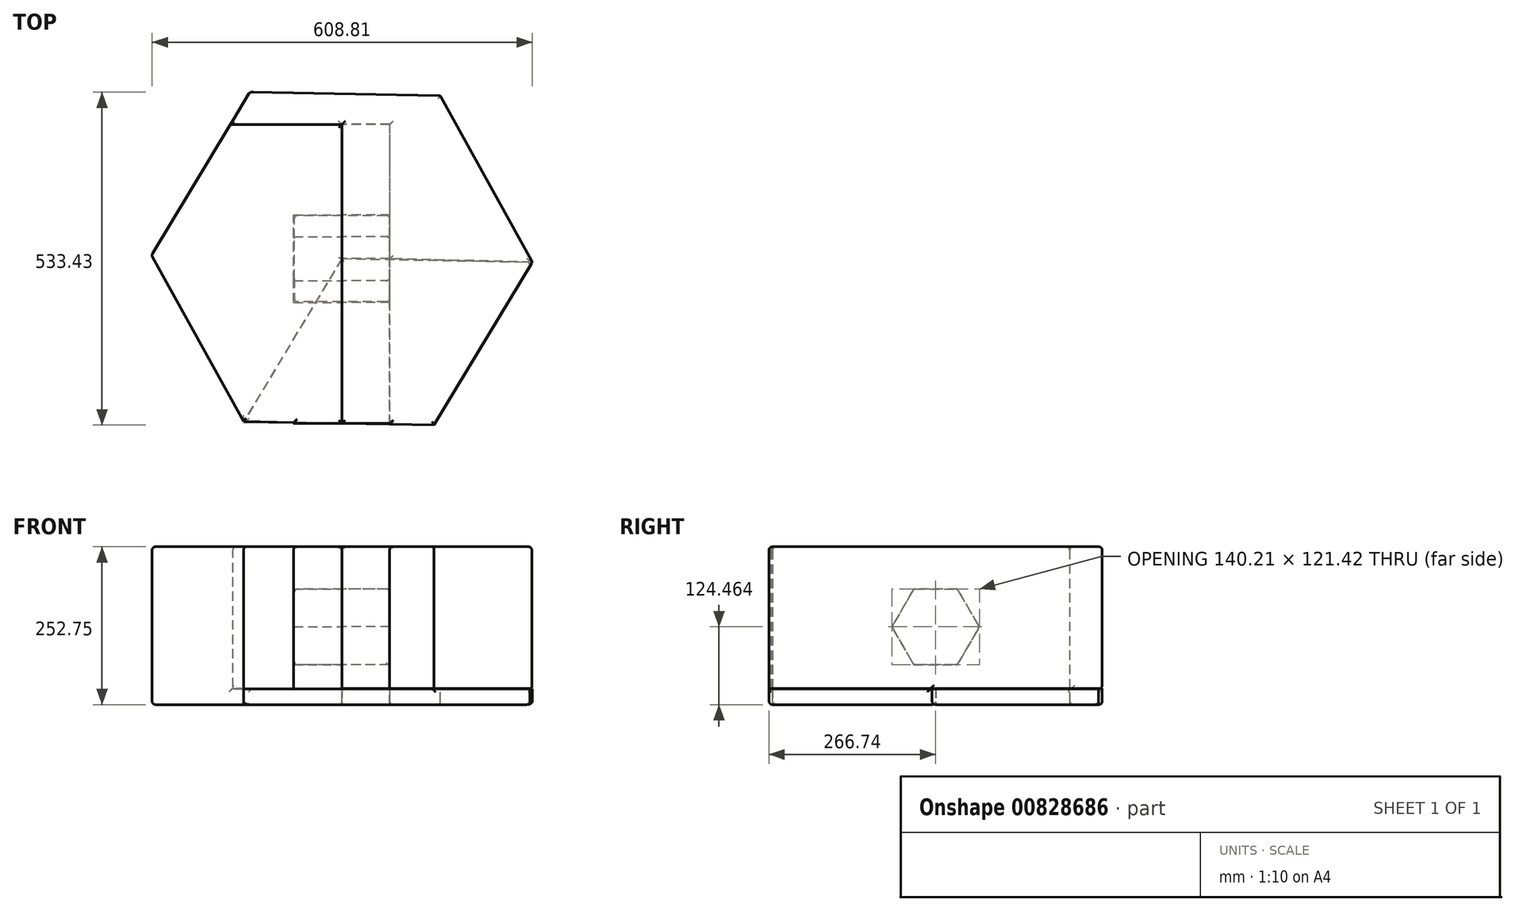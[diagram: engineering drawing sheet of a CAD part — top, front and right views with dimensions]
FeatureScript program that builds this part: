
annotation { "Feature Type Name" : "Feature", "Feature Type Description" : "" }
export const myFeature = defineFeature(function(context is Context, id is Id, definition is map)
    precondition{}
    {
        {
            var Q0;
            Q0=qCreatedBy(makeId("Top.planeOp"),FACE);
            var sketch = newSketch(context, id + "F0", { "sketchPlane" : qUnion([Q0])});
            skCircle(sketch, "E0.cCircle", {"center": v(0, 0) * mm, "radius": 264 * mm, "construction": true});
            skLineSegment(sketch, "E0.0", {"start": v(157.21, 261.19) * mm, "end": v(304.8, -5.56) * mm});
            skLineSegment(sketch, "E0.1", {"start": v(304.8, -5.56) * mm, "end": v(147.59, -266.74) * mm});
            skLineSegment(sketch, "E0.2", {"start": v(147.59, -266.74) * mm, "end": v(-157.21, -261.19) * mm});
            skLineSegment(sketch, "E0.3", {"start": v(-157.21, -261.19) * mm, "end": v(-304.8, 5.56) * mm});
            skLineSegment(sketch, "E0.4", {"start": v(-304.8, 5.56) * mm, "end": v(-147.59, 266.74) * mm});
            skLineSegment(sketch, "E0.5", {"start": v(-147.59, 266.74) * mm, "end": v(157.21, 261.19) * mm});
            skPoint(sketch, "E0.0.midPoint", {"position": v(231, 127.81) * mm});
            skSolve(sketch);
        }
        {
            var Q0;
            Q0=makeQuery(id+"F0.imprint","IMPRINT",FACE,{"disambiguationData":[TD([[makeQuery(id+"F0.imprint","IMPRINT",EDGE,{"derivedFrom":sQuery(id+"F0.wireOp",EDGE,"E0.0")}),-1.0]])]});
            var sketch = newSketch(context, id + "F1", { "sketchPlane" : qUnion([Q0])});
            skLineSegment(sketch, "E1", {"start": v(0, 0) * mm, "end": v(-157.21, -261.19) * mm});
            skLineSegment(sketch, "E2", {"start": v(0, 0) * mm, "end": v(304.8, -5.56) * mm});
            skLineSegment(sketch, "E3", {"start": v(304.8, -5.56) * mm, "end": v(147.59, -266.74) * mm});
            skLineSegment(sketch, "E4", {"start": v(147.59, -266.74) * mm, "end": v(-157.21, -261.19) * mm});
            skSolve(sketch);
        }
        {
            var Q0;
            Q0=makeQuery(id+"F1.imprint","IMPRINT",FACE,{"disambiguationData":[TD([[makeQuery(id+"F1.imprint","IMPRINT",EDGE,{"derivedFrom":sQuery(id+"F1.wireOp",EDGE,"E1")}),1.0]])]});
            extrude(context, id + "F2", {"entities" : qUnion([Q0]), "depth" : 25.4 * mm, "offsetDistance" : 25.4 * mm});
        }
        {
            var Q0;
            Q0=qCreatedBy(makeId("Right.planeOp"),FACE);
            var sketch = newSketch(context, id + "F3", { "sketchPlane" : qUnion([Q0])});
            skCircle(sketch, "E5.cCircle", {"center": v(0, 124.43) * mm, "radius": 60.5 * mm, "construction": true});
            skLineSegment(sketch, "E5.0", {"start": v(-34.92, 184.92) * mm, "end": v(34.92, 184.92) * mm});
            skLineSegment(sketch, "E5.1", {"start": v(34.92, 184.92) * mm, "end": v(69.85, 124.43) * mm});
            skLineSegment(sketch, "E5.2", {"start": v(69.85, 124.43) * mm, "end": v(34.93, 63.94) * mm});
            skLineSegment(sketch, "E5.3", {"start": v(34.93, 63.94) * mm, "end": v(-34.92, 63.94) * mm});
            skLineSegment(sketch, "E5.4", {"start": v(-34.92, 63.94) * mm, "end": v(-69.85, 124.43) * mm});
            skLineSegment(sketch, "E5.5", {"start": v(-69.85, 124.43) * mm, "end": v(-34.92, 184.92) * mm});
            skPoint(sketch, "E5.0.midPoint", {"position": v(0, 184.92) * mm});
            skSolve(sketch);
        }
        {
            var Q0;
            Q0 = qSketchRegion(id + "F3", true);
            extrude(context, id + "F4", {"entities" : qUnion([Q0]), "depth" : 76.2 * mm, "offsetDistance" : 25.4 * mm, "hasSecondDirection" : true, "secondDirectionOppositeDirection" : true, "secondDirectionDepth" : 76.2 * mm});
        }
        {
            var Q0;
            Q0=qCreatedBy(makeId("Right.planeOp"),FACE);
            var sketch = newSketch(context, id + "F5", { "sketchPlane" : qUnion([Q0])});
            skLineSegment(sketch, "E6", {"start": v(-264.07, 25.84) * mm, "end": v(0.25, 25.84) * mm});
            skLineSegment(sketch, "E7", {"start": v(0.25, 25.84) * mm, "end": v(0.25, 0) * mm});
            skLineSegment(sketch, "E8", {"start": v(0.25, 0) * mm, "end": v(214.97, 0) * mm});
            skLineSegment(sketch, "E9", {"start": v(214.97, 0) * mm, "end": v(214.97, 252.75) * mm});
            skLineSegment(sketch, "E10", {"start": v(214.97, 252.75) * mm, "end": v(-203.9, 252.75) * mm});
            skLineSegment(sketch, "E11", {"start": v(-203.9, 252.75) * mm, "end": v(-203.9, 88.98) * mm});
            skLineSegment(sketch, "E12", {"start": v(-203.9, 88.98) * mm, "end": v(-264.07, 88.98) * mm});
            skLineSegment(sketch, "E13", {"start": v(-264.07, 88.98) * mm, "end": v(-264.07, 25.84) * mm});
            skCircle(sketch, "E14.cCircle", {"center": v(0, 124.46) * mm, "radius": 60.71 * mm, "construction": true});
            skLineSegment(sketch, "E14.0", {"start": v(35.05, 185.18) * mm, "end": v(70.1, 124.46) * mm});
            skLineSegment(sketch, "E14.1", {"start": v(70.1, 124.46) * mm, "end": v(35.05, 63.75) * mm});
            skLineSegment(sketch, "E14.2", {"start": v(35.05, 63.75) * mm, "end": v(-35.05, 63.75) * mm});
            skLineSegment(sketch, "E14.3", {"start": v(-35.05, 63.75) * mm, "end": v(-70.1, 124.46) * mm});
            skLineSegment(sketch, "E14.4", {"start": v(-70.1, 124.46) * mm, "end": v(-35.05, 185.18) * mm});
            skLineSegment(sketch, "E14.5", {"start": v(-35.05, 185.18) * mm, "end": v(35.05, 185.18) * mm});
            skPoint(sketch, "E14.0.midPoint", {"position": v(52.58, 154.82) * mm});
            skSolve(sketch);
        }
        {
            var Q0;
            Q0=makeQuery(id+"F5.imprint","IMPRINT",FACE,{"disambiguationData":[TD([[makeQuery(id+"F5.imprint","IMPRINT",EDGE,{"derivedFrom":sQuery(id+"F5.wireOp",EDGE,"E6")}),1.0]])]});
            extrude(context, id + "F6", {"entities" : qUnion([Q0]), "depth" : 76.45 * mm, "offsetDistance" : 25.4 * mm});
        }
        {
            var Q0;
            Q0=makeQuery(id+"F6.opExtrude","SWEPT_FACE",FACE,{"disambiguationData":[OSD([sQuery(id+"F5.wireOp",EDGE,"E10")])]});
            var sketch = newSketch(context, id + "F7", { "sketchPlane" : qUnion([Q0])});
            skLineSegment(sketch, "E15", {"start": v(0, 214.97) * mm, "end": v(-178.75, 214.97) * mm});
            skLineSegment(sketch, "E16", {"start": v(-178.75, 214.97) * mm, "end": v(-147.59, 266.74) * mm});
            skLineSegment(sketch, "E17", {"start": v(-147.59, 266.74) * mm, "end": v(157.21, 261.19) * mm});
            skLineSegment(sketch, "E18", {"start": v(157.21, 261.19) * mm, "end": v(304.8, -5.56) * mm});
            skLineSegment(sketch, "E19", {"start": v(304.8, -5.56) * mm, "end": v(147.59, -266.74) * mm});
            skLineSegment(sketch, "E20", {"start": v(147.59, -266.74) * mm, "end": v(76.45, -265.45) * mm});
            skLineSegment(sketch, "E21", {"start": v(76.45, 214.97) * mm, "end": v(76.45, -265.45) * mm});
            skSolve(sketch);
        }
        {
            var Q0;
            Q0=makeQuery(id+"F7.imprint","IMPRINT",FACE,{"disambiguationData":[TD([[makeQuery(id+"F7.imprint","IMPRINT",EDGE,{"derivedFrom":sQuery(id+"F7.wireOp",EDGE,"E15")}),-1.0]])]});
            extrude(context, id + "F8", {"entities" : qUnion([Q0]), "operationType" : NewBodyOperationType.ADD, "oppositeDirection" : true, "depth" : 227.15 * mm, "offsetDistance" : 25.4 * mm});
        }
        {
            var Q0;
            Q0=makeQuery(id+"F2.opExtrude","CAP_FACE",FACE,{"disambiguationData":[OSD([sQuery(id+"F1.wireOp",EDGE,"E1"),sQuery(id+"F1.wireOp",EDGE,"E2"),sQuery(id+"F1.wireOp",EDGE,"E3"),sQuery(id+"F1.wireOp",EDGE,"E4")])],"isStart":false});
            var sketch = newSketch(context, id + "F9", { "sketchPlane" : qUnion([Q0])});
            skLineSegment(sketch, "E22", {"start": v(-157.34, -260.96) * mm, "end": v(-304.8, 5.56) * mm});
            skLineSegment(sketch, "E23", {"start": v(-304.8, 5.56) * mm, "end": v(-147.59, 266.74) * mm});
            skLineSegment(sketch, "E24", {"start": v(-147.59, 266.74) * mm, "end": v(157.21, 261.19) * mm});
            skLineSegment(sketch, "E25", {"start": v(157.21, 261.19) * mm, "end": v(304.8, -5.54) * mm});
            skLineSegment(sketch, "E26", {"start": v(304.8, -5.54) * mm, "end": v(76.7, 0) * mm});
            skLineSegment(sketch, "E27", {"start": v(76.7, 0) * mm, "end": v(76.7, 215.22) * mm});
            skLineSegment(sketch, "E28", {"start": v(76.7, 215.22) * mm, "end": v(-0.25, 215.22) * mm});
            skLineSegment(sketch, "E29", {"start": v(-0.25, 215.22) * mm, "end": v(-0.25, 0) * mm});
            skLineSegment(sketch, "E30", {"start": v(-0.25, 0) * mm, "end": v(-157.34, -260.96) * mm});
            skSolve(sketch);
        }
        {
            var Q0;
            Q0=makeQuery(id+"F9.imprint","IMPRINT",FACE,{"disambiguationData":[TD([[makeQuery(id+"F9.imprint","IMPRINT",EDGE,{"derivedFrom":sQuery(id+"F9.wireOp",EDGE,"E22")}),-1.0]])]});
            var Q1;
            Q1=makeQuery(id+"F2.opExtrude","CAP_FACE",FACE,{"disambiguationData":[OSD([sQuery(id+"F1.wireOp",EDGE,"E1"),sQuery(id+"F1.wireOp",EDGE,"E2"),sQuery(id+"F1.wireOp",EDGE,"E3"),sQuery(id+"F1.wireOp",EDGE,"E4")])],"isStart":true});
            extrude(context, id + "F10", {"entities" : qUnion([Q0]), "endBound" : BoundingType.UP_TO_SURFACE, "oppositeDirection" : true, "depth" : 25.4 * mm, "endBoundEntityFace" : qUnion([Q1]), "offsetDistance" : 25.4 * mm});
        }
        {
            var Q0;
            Q0=makeQuery(id+"F6.opExtrude","CAP_FACE",FACE,{"disambiguationData":[OSD([sQuery(id+"F5.wireOp",EDGE,"E6"),sQuery(id+"F5.wireOp",EDGE,"E7"),sQuery(id+"F5.wireOp",EDGE,"E8"),sQuery(id+"F5.wireOp",EDGE,"E9"),sQuery(id+"F5.wireOp",EDGE,"E10"),sQuery(id+"F5.wireOp",EDGE,"E11"),sQuery(id+"F5.wireOp",EDGE,"E12"),sQuery(id+"F5.wireOp",EDGE,"E13"),sQuery(id+"F5.wireOp",EDGE,"E14.0"),sQuery(id+"F5.wireOp",EDGE,"E14.1"),sQuery(id+"F5.wireOp",EDGE,"E14.2"),sQuery(id+"F5.wireOp",EDGE,"E14.3"),sQuery(id+"F5.wireOp",EDGE,"E14.4"),sQuery(id+"F5.wireOp",EDGE,"E14.5")])],"isStart":true});
            cPlane(context, id + "F11", {"entities" : qUnion([Q0]), "cplaneType" : CPlaneType.OFFSET, "offset" : 0.25 * mm, "width" : 152.4 * mm, "height" : 152.4 * mm});
        }
        {
            var Q0;
            Q0=qCreatedBy(id+"F11.planeOp",FACE);
            var sketch = newSketch(context, id + "F12", { "sketchPlane" : qUnion([Q0])});
            skLineSegment(sketch, "E31.bottom", {"start": v(-214.71, 252.75) * mm, "end": v(263.84, 252.75) * mm});
            skLineSegment(sketch, "E31.top", {"start": v(-214.71, 25.4) * mm, "end": v(263.84, 25.4) * mm});
            skLineSegment(sketch, "E31.left", {"start": v(-214.71, 252.75) * mm, "end": v(-214.71, 25.4) * mm});
            skLineSegment(sketch, "E31.right", {"start": v(263.84, 252.75) * mm, "end": v(263.84, 25.4) * mm});
            skCircle(sketch, "E32.cCircle", {"center": v(0, 124.46) * mm, "radius": 60.71 * mm, "construction": true});
            skLineSegment(sketch, "E32.0", {"start": v(-35.05, 185.18) * mm, "end": v(35.05, 185.18) * mm});
            skLineSegment(sketch, "E32.1", {"start": v(35.05, 185.18) * mm, "end": v(70.1, 124.46) * mm});
            skLineSegment(sketch, "E32.2", {"start": v(70.1, 124.46) * mm, "end": v(35.05, 63.75) * mm});
            skLineSegment(sketch, "E32.3", {"start": v(35.05, 63.75) * mm, "end": v(-35.05, 63.75) * mm});
            skLineSegment(sketch, "E32.4", {"start": v(-35.05, 63.75) * mm, "end": v(-70.1, 124.46) * mm});
            skLineSegment(sketch, "E32.5", {"start": v(-70.1, 124.46) * mm, "end": v(-35.05, 185.18) * mm});
            skPoint(sketch, "E32.0.midPoint", {"position": v(0, 185.18) * mm});
            skSolve(sketch);
        }
        {
            var Q0;
            Q0=makeQuery(id+"F12.imprint","IMPRINT",FACE,{"disambiguationData":[TD([[makeQuery(id+"F12.imprint","IMPRINT",EDGE,{"derivedFrom":sQuery(id+"F12.wireOp",EDGE,"E31.bottom")}),-1.0]])]});
            extrude(context, id + "F13", {"entities" : qUnion([Q0]), "depth" : 77.22 * mm, "offsetDistance" : 25.4 * mm});
        }
        {
            var Q0;
            Q0=makeQuery(id+"F10.opExtrude","CAP_FACE",FACE,{"disambiguationData":[OSD([sQuery(id+"F9.wireOp",EDGE,"E22"),sQuery(id+"F9.wireOp",EDGE,"E23"),sQuery(id+"F9.wireOp",EDGE,"E24"),sQuery(id+"F9.wireOp",EDGE,"E25"),sQuery(id+"F9.wireOp",EDGE,"E26"),sQuery(id+"F9.wireOp",EDGE,"E27"),sQuery(id+"F9.wireOp",EDGE,"E28"),sQuery(id+"F9.wireOp",EDGE,"E29"),sQuery(id+"F9.wireOp",EDGE,"E30")])],"isStart":true});
            var sketch = newSketch(context, id + "F14", { "sketchPlane" : qUnion([Q0])});
            skLineSegment(sketch, "E33", {"start": v(-304.8, 5.56) * mm, "end": v(-178.9, 214.71) * mm});
            skLineSegment(sketch, "E34", {"start": v(-178.9, 214.71) * mm, "end": v(-77.22, 214.71) * mm});
            skLineSegment(sketch, "E35", {"start": v(-77.22, 214.71) * mm, "end": v(-77.22, -262.42) * mm});
            skLineSegment(sketch, "E36", {"start": v(-157.34, -260.96) * mm, "end": v(-304.8, 5.56) * mm});
            skLineSegment(sketch, "E37", {"start": v(-77.22, -262.42) * mm, "end": v(-157.34, -260.96) * mm});
            skSolve(sketch);
        }
        {
            var Q0;
            Q0 = qSketchRegion(id + "F14", true);
            var Q1;
            Q1=makeQuery(id+"F13.opExtrude","SWEPT_FACE",FACE,{"disambiguationData":[OSD([sQuery(id+"F12.wireOp",EDGE,"E31.bottom")])]});
            extrude(context, id + "F15", {"entities" : qUnion([Q0]), "operationType" : NewBodyOperationType.ADD, "endBound" : BoundingType.UP_TO_SURFACE, "depth" : 25.4 * mm, "endBoundEntityFace" : qUnion([Q1]), "offsetDistance" : 25.4 * mm});
        }
        {
            var Q0;
            Q0=makeQuery(id+"F6.opExtrude","SWEPT_FACE",FACE,{"disambiguationData":[OSD([sQuery(id+"F5.wireOp",EDGE,"E12")])]});
            var sketch = newSketch(context, id + "F16", { "sketchPlane" : qUnion([Q0])});
            skLineSegment(sketch, "E38.bottom", {"start": v(0, -203.9) * mm, "end": v(76.45, -203.9) * mm});
            skLineSegment(sketch, "E38.top", {"start": v(0, -264.07) * mm, "end": v(76.45, -264.07) * mm});
            skLineSegment(sketch, "E38.left", {"start": v(0, -203.9) * mm, "end": v(0, -264.07) * mm});
            skLineSegment(sketch, "E38.right", {"start": v(76.45, -203.9) * mm, "end": v(76.45, -264.07) * mm});
            skSolve(sketch);
        }
        {
            var Q0;
            Q0 = qSketchRegion(id + "F16", true);
            var Q1;
            Q1=makeQuery(id+"F2.opExtrude","CAP_FACE",FACE,{"disambiguationData":[OSD([sQuery(id+"F1.wireOp",EDGE,"E1"),sQuery(id+"F1.wireOp",EDGE,"E2"),sQuery(id+"F1.wireOp",EDGE,"E3"),sQuery(id+"F1.wireOp",EDGE,"E4")])],"isStart":true});
            var Q2;
            Q2=makeQuery(id+"F8.opExtrude","CAP_VERTEX",VERTEX,{"disambiguationData":[OSD([sQuery(id+"F7.wireOp",EDGE,"E20"),sQuery(id+"F7.wireOp",EDGE,"E21")])],"isStart":true});
            extrude(context, id + "F17", {"entities" : qUnion([Q0]), "operationType" : NewBodyOperationType.ADD, "endBound" : BoundingType.UP_TO_VERTEX, "depth" : 25.4 * mm, "endBoundEntityFace" : qUnion([Q1]), "endBoundEntityVertex" : qUnion([Q2]), "offsetDistance" : 25.4 * mm});
        }
        {
            var Q0;
            Q0=makeQuery(id+"F15.boolean.opBoolean","MERGE",FACE,{"derivedFrom":[makeQuery(id+"F13.opExtrude","SWEPT_FACE",FACE,{"disambiguationData":[OSD([sQuery(id+"F12.wireOp",EDGE,"E31.bottom")])]}),makeQuery(id+"F15.opExtrude","CAP_FACE",FACE,{"disambiguationData":[OSD([sQuery(id+"F14.wireOp",EDGE,"E33"),sQuery(id+"F14.wireOp",EDGE,"E34"),sQuery(id+"F14.wireOp",EDGE,"E35"),sQuery(id+"F14.wireOp",EDGE,"E36"),sQuery(id+"F14.wireOp",EDGE,"E37")])],"isStart":false})]});
            var Q1;
            Q1=makeQuery(id+"F15.boolean.opBoolean","MERGE",FACE,{"derivedFrom":[makeQuery(id+"F10.opExtrude","SWEPT_FACE",FACE,{"disambiguationData":[OSD([sQuery(id+"F9.wireOp",EDGE,"E23")])]}),makeQuery(id+"F15.opExtrude","SWEPT_FACE",FACE,{"disambiguationData":[OSD([sQuery(id+"F14.wireOp",EDGE,"E33")])]})]});
            var Q2;
            Q2=makeQuery(id+"F8.opExtrude","SWEPT_FACE",FACE,{"disambiguationData":[OSD([sQuery(id+"F7.wireOp",EDGE,"E17")])]});
            var Q3;
            Q3=makeQuery(id+"F8.opExtrude","SWEPT_FACE",FACE,{"disambiguationData":[OSD([sQuery(id+"F7.wireOp",EDGE,"E16")])]});
            var Q4;
            {var subQ0=sQuery(id+"F5.wireOp",EDGE,"E10");Q4=makeQuery(id+"F17.boolean.opBoolean","MERGE",FACE,{"derivedFrom":[makeQuery(id+"F8.boolean.opBoolean","MERGE",FACE,{"derivedFrom":[makeQuery(id+"F6.opExtrude","SWEPT_FACE",FACE,{"disambiguationData":[OSD([subQ0])]}),makeQuery(id+"F8.opExtrude","CAP_FACE",FACE,{"disambiguationData":[OSD([sQuery(id+"F5.wireOp",EDGE,"E9"),subQ0,sQuery(id+"F7.wireOp",EDGE,"E15"),sQuery(id+"F7.wireOp",EDGE,"E16"),sQuery(id+"F7.wireOp",EDGE,"E17"),sQuery(id+"F7.wireOp",EDGE,"E18"),sQuery(id+"F7.wireOp",EDGE,"E19"),sQuery(id+"F7.wireOp",EDGE,"E20"),sQuery(id+"F7.wireOp",EDGE,"E21")])],"isStart":true})]}),makeQuery(id+"F17.opExtrude","CAP_FACE",FACE,{"disambiguationData":[OSD([sQuery(id+"F16.wireOp",EDGE,"E38.bottom"),sQuery(id+"F16.wireOp",EDGE,"E38.top"),sQuery(id+"F16.wireOp",EDGE,"E38.left"),sQuery(id+"F16.wireOp",EDGE,"E38.right")])],"isStart":false})]});}
            var Q5;
            Q5=makeQuery(id+"F8.opExtrude","SWEPT_FACE",FACE,{"disambiguationData":[OSD([sQuery(id+"F7.wireOp",EDGE,"E18")])]});
            var Q6;
            Q6=makeQuery(id+"F10.opExtrude","CAP_FACE",FACE,{"disambiguationData":[OSD([sQuery(id+"F9.wireOp",EDGE,"E22"),sQuery(id+"F9.wireOp",EDGE,"E23"),sQuery(id+"F9.wireOp",EDGE,"E24"),sQuery(id+"F9.wireOp",EDGE,"E25"),sQuery(id+"F9.wireOp",EDGE,"E26"),sQuery(id+"F9.wireOp",EDGE,"E27"),sQuery(id+"F9.wireOp",EDGE,"E28"),sQuery(id+"F9.wireOp",EDGE,"E29"),sQuery(id+"F9.wireOp",EDGE,"E30")])],"isStart":false});
            var Q7;
            Q7=makeQuery(id+"F2.opExtrude","CAP_FACE",FACE,{"disambiguationData":[OSD([sQuery(id+"F1.wireOp",EDGE,"E1"),sQuery(id+"F1.wireOp",EDGE,"E2"),sQuery(id+"F1.wireOp",EDGE,"E3"),sQuery(id+"F1.wireOp",EDGE,"E4")])],"isStart":true});
            var Q8;
            Q8=makeQuery(id+"F2.opExtrude","SWEPT_FACE",FACE,{"disambiguationData":[OSD([sQuery(id+"F1.wireOp",EDGE,"E3")])]});
            fillet(context, id + "F18", {"entities" : qUnion([Q0, Q1, Q2, Q3, Q4, Q5, Q6, Q7, Q8]), "radius" : 5.08 * mm, "tangentPropagation" : true, "allowEdgeOverflow" : false});
        }
        {
            var Q0;
            Q0=makeQuery(id+"F15.boolean.opBoolean","MERGE",FACE,{"derivedFrom":[makeQuery(id+"F13.opExtrude","SWEPT_FACE",FACE,{"disambiguationData":[OSD([sQuery(id+"F12.wireOp",EDGE,"E31.bottom")])]}),makeQuery(id+"F15.opExtrude","CAP_FACE",FACE,{"disambiguationData":[OSD([sQuery(id+"F14.wireOp",EDGE,"E33"),sQuery(id+"F14.wireOp",EDGE,"E34"),sQuery(id+"F14.wireOp",EDGE,"E35"),sQuery(id+"F14.wireOp",EDGE,"E36"),sQuery(id+"F14.wireOp",EDGE,"E37")])],"isStart":false})]});
            cPlane(context, id + "F19", {"entities" : qUnion([Q0]), "cplaneType" : CPlaneType.OFFSET, "offset" : 0 * mm, "width" : 152.4 * mm, "height" : 152.4 * mm});
        }
        {
            var Q0;
            Q0=makeQuery(id+"F4.opExtrude","SWEPT_FACE",FACE,{"disambiguationData":[OSD([sQuery(id+"F3.wireOp",EDGE,"E5.0")])]});
            var Q1;
            Q1=makeQuery(id+"F4.opExtrude","CAP_FACE",FACE,{"disambiguationData":[OSD([sQuery(id+"F3.wireOp",EDGE,"E5.0"),sQuery(id+"F3.wireOp",EDGE,"E5.1"),sQuery(id+"F3.wireOp",EDGE,"E5.2"),sQuery(id+"F3.wireOp",EDGE,"E5.3"),sQuery(id+"F3.wireOp",EDGE,"E5.4"),sQuery(id+"F3.wireOp",EDGE,"E5.5")])],"isStart":true});
            var Q2;
            Q2=makeQuery(id+"F4.opExtrude","SWEPT_FACE",FACE,{"disambiguationData":[OSD([sQuery(id+"F3.wireOp",EDGE,"E5.5")])]});
            var Q3;
            Q3=makeQuery(id+"F4.opExtrude","SWEPT_FACE",FACE,{"disambiguationData":[OSD([sQuery(id+"F3.wireOp",EDGE,"E5.1")])]});
            var Q4;
            Q4=makeQuery(id+"F4.opExtrude","SWEPT_FACE",FACE,{"disambiguationData":[OSD([sQuery(id+"F3.wireOp",EDGE,"E5.4")])]});
            var Q5;
            Q5=makeQuery(id+"F4.opExtrude","SWEPT_FACE",FACE,{"disambiguationData":[OSD([sQuery(id+"F3.wireOp",EDGE,"E5.2")])]});
            fillet(context, id + "F20", {"entities" : qUnion([Q0, Q1, Q2, Q3, Q4, Q5]), "radius" : 5.08 * mm, "tangentPropagation" : true, "allowEdgeOverflow" : false});
        }
    });
